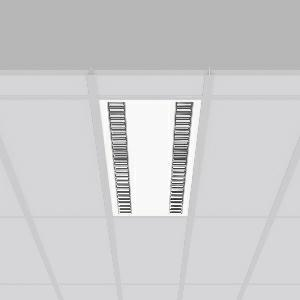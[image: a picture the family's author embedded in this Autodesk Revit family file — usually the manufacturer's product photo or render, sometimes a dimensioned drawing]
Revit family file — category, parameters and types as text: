
# Revit family: sonis_901680_002_1_6861
name_source: partatom
category: Lighting Fixtures
units: mm (PartAtom-declared; Revit-internal decimal feet)

## family parameters
Cut with Voids When Loaded = No
Host = Face
Light Source = No
Part Type = Normal
Room Calculation Point = No
Round Connector Dimension = Use Diameter
Shared = No

## types (1)
- SONIS (1 x LED Modul 840, 6500 lm, 4000)
    Apparent Load = 50 VA
    CIE Flux Codes = 83 100 100 100 100
    Color Rendering = 80
    Color Temperature = 4000
    Default Elevation = 1800 mm
    Description = Series: SONIS
High-efficiency lay-in luminaire for ceiling systems with visible mounting rails. Housing: metal, powder-coated. Alea optical system: Reflector structure (ABS, Aluminium-coated, highly polished) with integrated diffuser made of non-yellowing plastic (PMMA) opal for glare-free light at the workstation. Narrow beam, brilliant luminous effect. Suitable for Recessed ceiling mounting. Driver integrated. Perfect for office areas (RUG < 19) and environments with computer screens in accordance with EN 12464-1. 
Colour: white
Length: 1197 mm
Width: 297 mm
Cut-out length: 1175 mm
Cut-out width: 275 mm
Recess height: 27 mm
Lamp: LED
Socket: without socket
Colour temperature: 4000K
Colour rendering index (CRI): 80
System power: 50 W
Rated luminous flux: 6500 lm
Luminous efficiency: 130 lm/W
Control gear: Regulated power supply
Protection class: I
Type of protection: IP 20
    Height = 0 mm  [stored 0 ft]
    Lamp = 1 x LED Modul 840
    Lamp Light Flux = 6500 lm
    Lamp count = 1
    Length = 1197 mm
    Lifetime = 50000 h
    Luminous efficacy = 130 lm/W
    Manufacturer = RZB
    ModVariant = No
    Model = 901680.002.1
    Mounting Place = Ceiling
    Mounting Type = Recessed
    Number of Poles = 1
    OnlyDefault = Yes
    Power Factor = 1
    Product Name = SONIS
    Product group = Recessed modular luminaires
    ProductGroupID = 406
    Protection Class = Protection class I
    Protection Degree = IP 20
    RLX_Detail_Level = 1
    RLX_Emergency_Light_Flux = 0 lm
    RLX_Emergency_Type = 0
    RLX_Emergency_Type_DB = No
    RlxData = <blob elided: 37029 chars, md5=89a8cfa5>
    Socket = socket
    Standby Power = 0 W
    System Light Flux = 6500 lm
    System Power = 50 W
    Type Comments = Product without accessories
    Type Image = 901648.002.jpg
    URL = http://relux.com
    VarID = ---
    Voltage = 230 V
    Voltage Range = 220-240 V
    Weight = 0.00 kg
    Width = 297 mm

note: [stored X ft] marks values corroborated as IEEE doubles in the binary element streams (Revit-internal decimal feet)

## geometry (parser evidence)
native form markers: Blend x4, Sweep x10
no freeform markers — native parametric forms only
